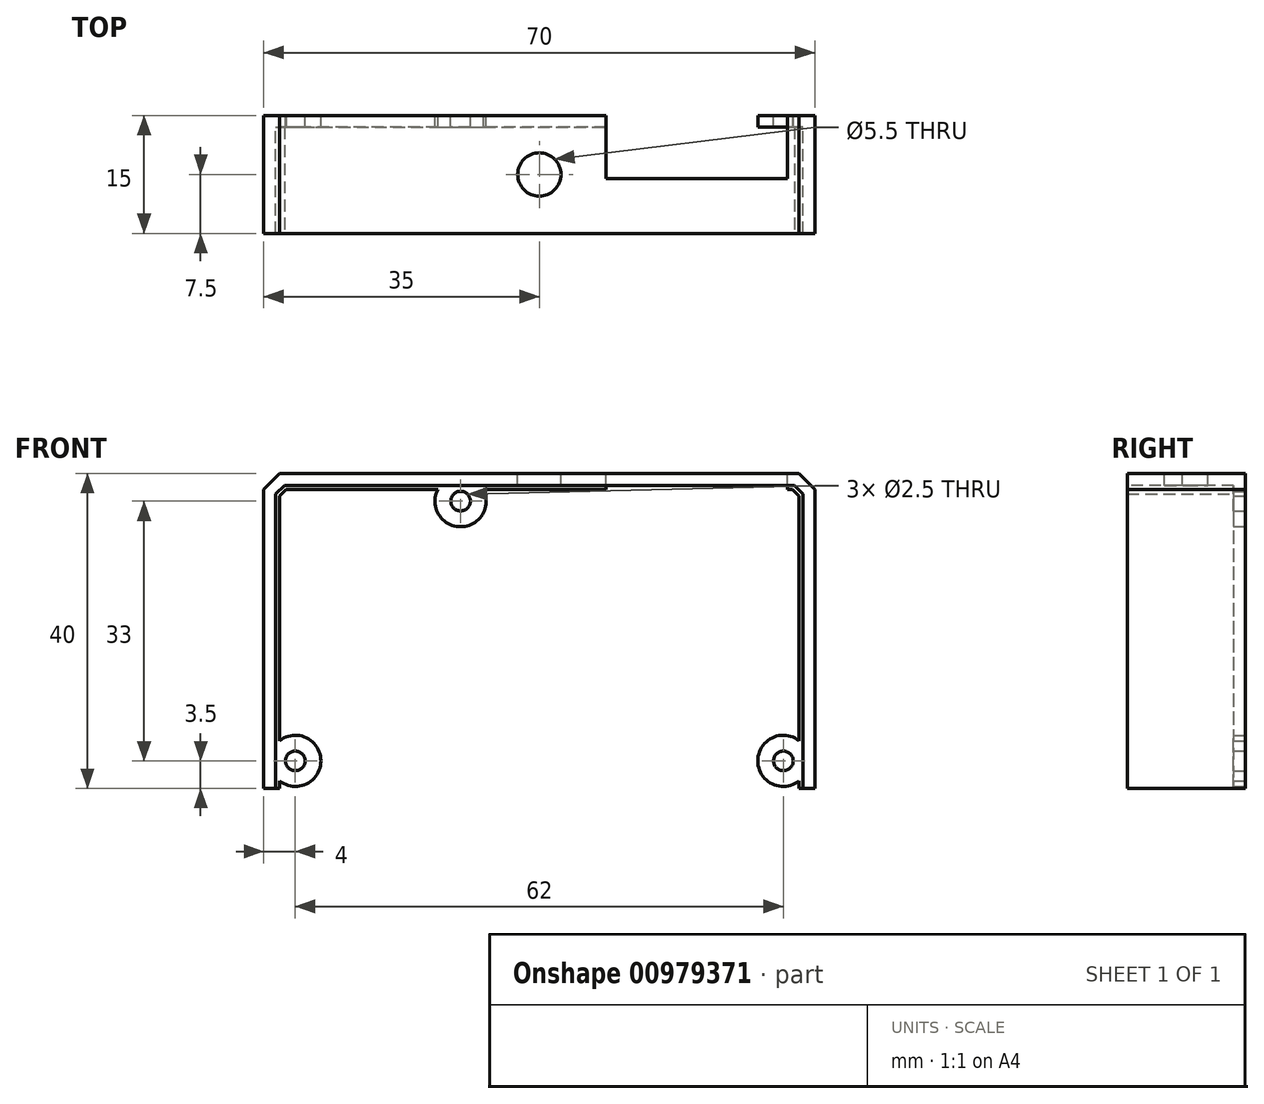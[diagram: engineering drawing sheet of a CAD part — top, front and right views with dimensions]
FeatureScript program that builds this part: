
annotation { "Feature Type Name" : "Feature", "Feature Type Description" : "" }
export const myFeature = defineFeature(function(context is Context, id is Id, definition is map)
    precondition{}
    {
        {
            var Q0;
            Q0=qCreatedBy(makeId("Front.planeOp"),FACE);
            var sketch = newSketch(context, id + "F0", { "sketchPlane" : qUnion([Q0])});
            skLineSegment(sketch, "E0.bottom", {"start": v(-35, 20) * mm, "end": v(35, 20) * mm});
            skLineSegment(sketch, "E0.top", {"start": v(-35, -20) * mm, "end": v(35, -20) * mm});
            skLineSegment(sketch, "E0.left", {"start": v(-35, 20) * mm, "end": v(-35, -20) * mm});
            skLineSegment(sketch, "E0.right", {"start": v(35, 20) * mm, "end": v(35, -20) * mm});
            skCircle(sketch, "E1", {"center": v(-10, 16.5) * mm, "radius": 1.25 * mm});
            skLineSegment(sketch, "E2.bottom", {"start": v(-31, 16.5) * mm, "end": v(31, 16.5) * mm, "construction": true});
            skLineSegment(sketch, "E2.top", {"start": v(-31, -16.5) * mm, "end": v(31, -16.5) * mm, "construction": true});
            skLineSegment(sketch, "E2.left", {"start": v(-31, 16.5) * mm, "end": v(-31, -16.5) * mm, "construction": true});
            skLineSegment(sketch, "E2.right", {"start": v(31, 16.5) * mm, "end": v(31, -16.5) * mm, "construction": true});
            skCircle(sketch, "E3", {"center": v(-31, -16.5) * mm, "radius": 1.25 * mm});
            skCircle(sketch, "E4", {"center": v(31, -16.5) * mm, "radius": 1.25 * mm});
            skSolve(sketch);
        }
        {
            var Q0;
            Q0=makeQuery(id+"F0.imprint","IMPRINT",FACE,{"disambiguationData":[TD([[makeQuery(id+"F0.imprint","IMPRINT",EDGE,{"derivedFrom":sQuery(id+"F0.wireOp",EDGE,"E0.bottom")}),-1.0]])]});
            extrude(context, id + "F1", {"entities" : qUnion([Q0]), "depth" : 15 * mm, "offsetDistance" : 25 * mm});
        }
        {
            var Q0;
            Q0=makeQuery(id+"F1.opExtrude","SWEPT_EDGE",EDGE,{"disambiguationData":[OSD([sQuery(id+"F0.wireOp",EDGE,"E0.bottom"),sQuery(id+"F0.wireOp",EDGE,"E0.left")])]});
            var Q1;
            Q1=makeQuery(id+"F1.opExtrude","SWEPT_EDGE",EDGE,{"disambiguationData":[OSD([sQuery(id+"F0.wireOp",EDGE,"E0.bottom"),sQuery(id+"F0.wireOp",EDGE,"E0.right")])]});
            chamfer(context, id + "F2", {"entities" : qUnion([Q0, Q1]), "width" : 2 * mm, "tangentPropagation" : true});
        }
        {
            var Q0;
            Q0=makeQuery(id+"F1.opExtrude","SWEPT_FACE",FACE,{"disambiguationData":[OSD([sQuery(id+"F0.wireOp",EDGE,"E1")])]});
            var Q1;
            Q1=makeQuery(id+"F1.opExtrude","SWEPT_FACE",FACE,{"disambiguationData":[OSD([sQuery(id+"F0.wireOp",EDGE,"E3")])]});
            var Q2;
            Q2=makeQuery(id+"F1.opExtrude","SWEPT_FACE",FACE,{"disambiguationData":[OSD([sQuery(id+"F0.wireOp",EDGE,"E4")])]});
            var Q3;
            Q3=makeQuery(id+"F1.opExtrude","SWEPT_FACE",FACE,{"disambiguationData":[OSD([sQuery(id+"F0.wireOp",EDGE,"E0.top")])]});
            var Q4;
            Q4=makeQuery(id+"F1.opExtrude","CAP_FACE",FACE,{"disambiguationData":[OSD([sQuery(id+"F0.wireOp",EDGE,"E0.bottom"),sQuery(id+"F0.wireOp",EDGE,"E0.top"),sQuery(id+"F0.wireOp",EDGE,"E0.left"),sQuery(id+"F0.wireOp",EDGE,"E0.right"),sQuery(id+"F0.wireOp",EDGE,"E1"),sQuery(id+"F0.wireOp",EDGE,"E3"),sQuery(id+"F0.wireOp",EDGE,"E4")])],"isStart":false});
            shell(context, id + "F3", {"entities" : qUnion([Q0, Q1, Q2, Q3, Q4]), "thickness" : 1.5 * mm});
        }
        {
            var Q0;
            Q0=makeQuery(id+"F1.opExtrude","CAP_FACE",FACE,{"disambiguationData":[OSD([sQuery(id+"F0.wireOp",EDGE,"E0.bottom"),sQuery(id+"F0.wireOp",EDGE,"E0.top"),sQuery(id+"F0.wireOp",EDGE,"E0.left"),sQuery(id+"F0.wireOp",EDGE,"E0.right"),sQuery(id+"F0.wireOp",EDGE,"E1"),sQuery(id+"F0.wireOp",EDGE,"E3"),sQuery(id+"F0.wireOp",EDGE,"E4")])],"isStart":true});
            var Q1;
            Q1=makeQuery(id+"F3.opShell","OFFSET_FACE",FACE,{"disambiguationData":[OSD([sQuery(id+"F0.wireOp",EDGE,"E0.bottom"),sQuery(id+"F0.wireOp",EDGE,"E0.top"),sQuery(id+"F0.wireOp",EDGE,"E0.left"),sQuery(id+"F0.wireOp",EDGE,"E0.right"),sQuery(id+"F0.wireOp",EDGE,"E1"),sQuery(id+"F0.wireOp",EDGE,"E3"),sQuery(id+"F0.wireOp",EDGE,"E4")])]});
            var Q2;
            Q2=makeQuery(id+"F1.opExtrude","SWEPT_FACE",FACE,{"disambiguationData":[OSD([sQuery(id+"F0.wireOp",EDGE,"E0.top")])]});
            shell(context, id + "F4", {"entities" : qUnion([Q0, Q1, Q2]), "thickness" : 2 * mm});
        }
        {
            var Q0;
            Q0=makeQuery(id+"F1.opExtrude","SWEPT_FACE",FACE,{"disambiguationData":[OSD([sQuery(id+"F0.wireOp",EDGE,"E0.bottom")])]});
            var sketch = newSketch(context, id + "F5", { "sketchPlane" : qUnion([Q0])});
            skCircle(sketch, "E5", {"center": v(0, -7.5) * mm, "radius": 2.75 * mm});
            skLineSegment(sketch, "E6", {"start": v(0, 0) * mm, "end": v(0, -15) * mm, "construction": true});
            skLineSegment(sketch, "E7", {"start": v(8.5, 0) * mm, "end": v(8.5, -8) * mm});
            skLineSegment(sketch, "E8", {"start": v(8.5, -8) * mm, "end": v(31.5, -8) * mm});
            skLineSegment(sketch, "E9", {"start": v(31.5, -8) * mm, "end": v(31.5, 0) * mm});
            skPoint(sketch, "E10", {"position": v(20, -8) * mm});
            skSolve(sketch);
        }
        {
            var Q0;
            Q0=makeQuery(id+"F5.imprint","IMPRINT",FACE,{"disambiguationData":[TD([[makeQuery(id+"F5.imprint","IMPRINT",EDGE,{"derivedFrom":sQuery(id+"F5.wireOp",EDGE,"E5")}),1.0]])]});
            var Q1;
            {var subQ0=sQuery(id+"F5.wireOp",EDGE,"E7");Q1=makeQuery(id+"F5.imprint","IMPRINT",FACE,{"disambiguationData":[TD([[makeQuery(id+"F5.imprint","IMPRINT",EDGE,{"derivedFrom":subQ0}),1.0]])]});}
            extrude(context, id + "F6", {"entities" : qUnion([Q0, Q1]), "operationType" : NewBodyOperationType.REMOVE, "oppositeDirection" : true, "depth" : 25 * mm, "offsetDistance" : 25 * mm});
        }
    });
